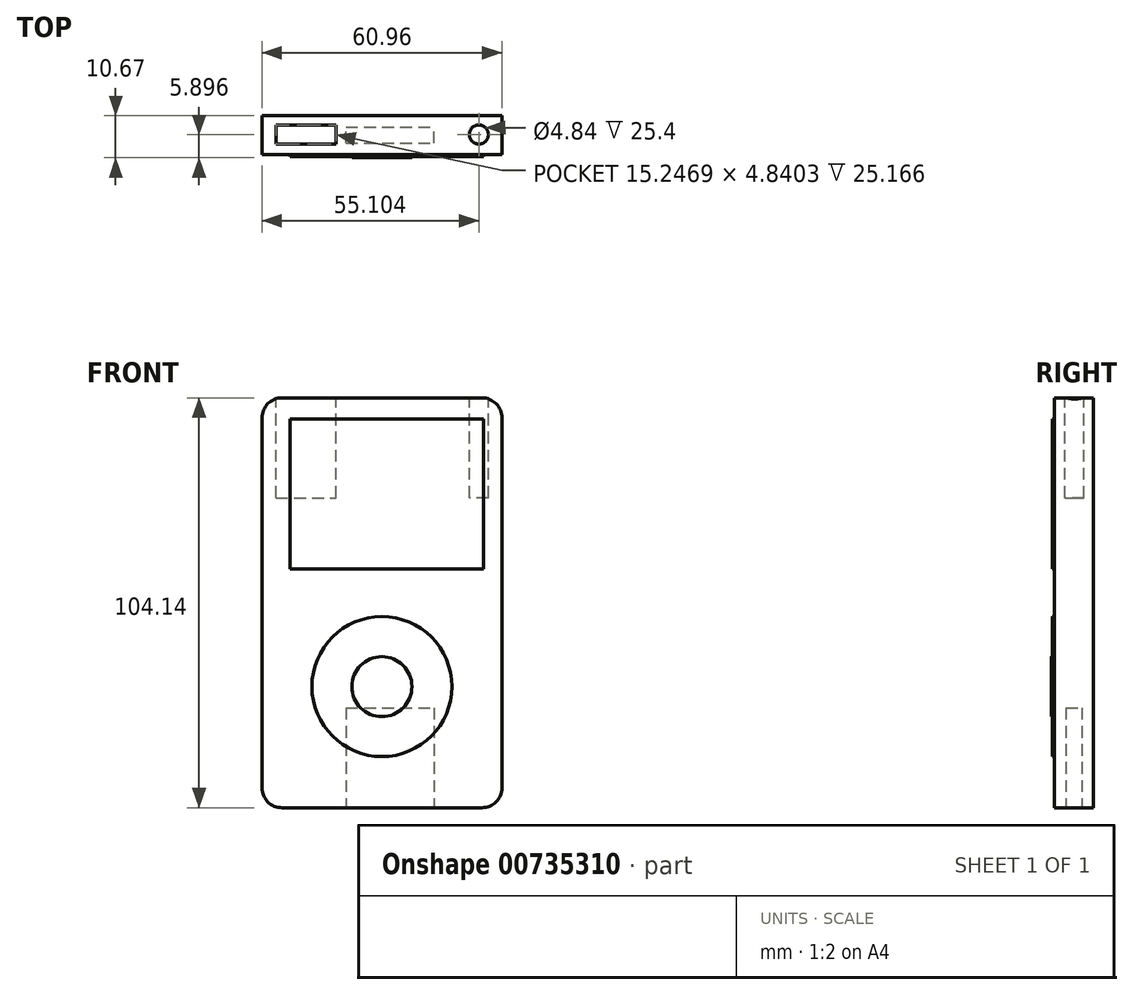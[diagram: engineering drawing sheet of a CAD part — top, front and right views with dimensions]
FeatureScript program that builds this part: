
annotation { "Feature Type Name" : "Feature", "Feature Type Description" : "" }
export const myFeature = defineFeature(function(context is Context, id is Id, definition is map)
    precondition{}
    {
        {
            var Q0;
            Q0=qCreatedBy(makeId("Front.planeOp"),FACE);
            var sketch = newSketch(context, id + "F0", { "sketchPlane" : qUnion([Q0])});
            skLineSegment(sketch, "E0.bottom", {"start": v(-21.34, 52.79) * mm, "end": v(39.62, 52.79) * mm});
            skLineSegment(sketch, "E0.top", {"start": v(-21.34, -51.35) * mm, "end": v(39.62, -51.35) * mm});
            skLineSegment(sketch, "E0.left", {"start": v(-21.34, 52.79) * mm, "end": v(-21.34, -51.35) * mm});
            skLineSegment(sketch, "E0.right", {"start": v(39.62, 52.79) * mm, "end": v(39.62, -51.35) * mm});
            skSolve(sketch);
        }
        {
            var Q0;
            Q0=makeQuery(id+"F0.imprint","IMPRINT",FACE,{"disambiguationData":[TD([[makeQuery(id+"F0.imprint","IMPRINT",EDGE,{"derivedFrom":sQuery(id+"F0.wireOp",EDGE,"E0.bottom")}),-1.0]])]});
            extrude(context, id + "F1", {"entities" : qUnion([Q0]), "depth" : 10.4 * mm, "offsetDistance" : 25.4 * mm});
        }
        {
            var Q0;
            Q0=makeQuery(id+"F1.opExtrude","CAP_FACE",FACE,{"disambiguationData":[OSD([sQuery(id+"F0.wireOp",EDGE,"E0.bottom"),sQuery(id+"F0.wireOp",EDGE,"E0.top"),sQuery(id+"F0.wireOp",EDGE,"E0.left"),sQuery(id+"F0.wireOp",EDGE,"E0.right")])],"isStart":false});
            var sketch = newSketch(context, id + "F2", { "sketchPlane" : qUnion([Q0])});
            skCircle(sketch, "E1", {"center": v(9.14, -20.58) * mm, "radius": 17.78 * mm});
            skLineSegment(sketch, "E2.bottom", {"start": v(-14.25, 47.45) * mm, "end": v(34.97, 47.45) * mm});
            skLineSegment(sketch, "E2.top", {"start": v(-14.25, 9.35) * mm, "end": v(34.97, 9.35) * mm});
            skLineSegment(sketch, "E2.left", {"start": v(-14.25, 47.45) * mm, "end": v(-14.25, 9.35) * mm});
            skLineSegment(sketch, "E2.right", {"start": v(34.97, 47.45) * mm, "end": v(34.97, 9.35) * mm});
            skSolve(sketch);
        }
        {
            var Q0;
            Q0=makeQuery(id+"F2.imprint","IMPRINT",FACE,{"disambiguationData":[TD([[makeQuery(id+"F2.imprint","IMPRINT",EDGE,{"derivedFrom":sQuery(id+"F2.wireOp",EDGE,"E1")}),-1.0]])]});
            extrude(context, id + "F3", {"entities" : qUnion([Q0]), "operationType" : NewBodyOperationType.REMOVE, "oppositeDirection" : true, "depth" : 0.5 * mm, "offsetDistance" : 25.4 * mm});
        }
        {
            var Q0;
            Q0=makeQuery(id+"F3.boolean.opBoolean","SPLIT",FACE,{"disambiguationData":[TD([makeQuery(id+"F3.opExtrude","SWEPT_FACE",FACE,{"disambiguationData":[OSD([sQuery(id+"F2.wireOp",EDGE,"E1")])]})])],"derivedFrom":makeQuery(id+"F1.opExtrude","CAP_FACE",FACE,{"disambiguationData":[OSD([sQuery(id+"F0.wireOp",EDGE,"E0.bottom"),sQuery(id+"F0.wireOp",EDGE,"E0.top"),sQuery(id+"F0.wireOp",EDGE,"E0.left"),sQuery(id+"F0.wireOp",EDGE,"E0.right")])],"isStart":false})});
            var sketch = newSketch(context, id + "F4", { "sketchPlane" : qUnion([Q0])});
            skCircle(sketch, "E3", {"center": v(9.14, -20.58) * mm, "radius": 7.62 * mm});
            skSolve(sketch);
        }
        {
            var Q0;
            Q0 = qSketchRegion(id + "F4", true);
            extrude(context, id + "F5", {"entities" : qUnion([Q0]), "operationType" : NewBodyOperationType.ADD, "depth" : 0.25 * mm, "offsetDistance" : 25.4 * mm});
        }
        {
            var Q0;
            Q0=makeQuery(id+"F1.opExtrude","SWEPT_FACE",FACE,{"disambiguationData":[OSD([sQuery(id+"F0.wireOp",EDGE,"E0.bottom")])]});
            var sketch = newSketch(context, id + "F6", { "sketchPlane" : qUnion([Q0])});
            skLineSegment(sketch, "E4.bottom", {"start": v(-17.79, -2.35) * mm, "end": v(-2.54, -2.35) * mm});
            skLineSegment(sketch, "E4.top", {"start": v(-17.79, -7.2) * mm, "end": v(-2.54, -7.2) * mm});
            skLineSegment(sketch, "E4.left", {"start": v(-17.79, -2.35) * mm, "end": v(-17.79, -7.2) * mm});
            skLineSegment(sketch, "E4.right", {"start": v(-2.54, -2.35) * mm, "end": v(-2.54, -7.2) * mm});
            skCircle(sketch, "E5", {"center": v(33.76, -4.77) * mm, "radius": 2.42 * mm});
            skSolve(sketch);
        }
        {
            var Q0;
            Q0=makeQuery(id+"F6.imprint","IMPRINT",FACE,{"disambiguationData":[TD([[makeQuery(id+"F6.imprint","IMPRINT",EDGE,{"derivedFrom":sQuery(id+"F6.wireOp",EDGE,"E4.bottom")}),-1.0]])]});
            var Q1;
            Q1=makeQuery(id+"F6.imprint","IMPRINT",FACE,{"disambiguationData":[TD([[makeQuery(id+"F6.imprint","IMPRINT",EDGE,{"derivedFrom":sQuery(id+"F6.wireOp",EDGE,"E5")}),1.0]])]});
            extrude(context, id + "F7", {"entities" : qUnion([Q0, Q1]), "operationType" : NewBodyOperationType.REMOVE, "oppositeDirection" : true, "depth" : 25.4 * mm, "offsetDistance" : 25.4 * mm});
        }
        {
            var Q0;
            Q0=makeQuery(id+"F1.opExtrude","SWEPT_EDGE",EDGE,{"disambiguationData":[OSD([sQuery(id+"F0.wireOp",EDGE,"E0.top"),sQuery(id+"F0.wireOp",EDGE,"E0.right")])]});
            var Q1;
            Q1=makeQuery(id+"F1.opExtrude","SWEPT_EDGE",EDGE,{"disambiguationData":[OSD([sQuery(id+"F0.wireOp",EDGE,"E0.top"),sQuery(id+"F0.wireOp",EDGE,"E0.left")])]});
            var Q2;
            Q2=makeQuery(id+"F1.opExtrude","SWEPT_EDGE",EDGE,{"disambiguationData":[OSD([sQuery(id+"F0.wireOp",EDGE,"E0.bottom"),sQuery(id+"F0.wireOp",EDGE,"E0.left")])]});
            var Q3;
            Q3=makeQuery(id+"F1.opExtrude","SWEPT_EDGE",EDGE,{"disambiguationData":[OSD([sQuery(id+"F0.wireOp",EDGE,"E0.bottom"),sQuery(id+"F0.wireOp",EDGE,"E0.right")])]});
            fillet(context, id + "F8", {"entities" : qUnion([Q0, Q1, Q2, Q3]), "radius" : 5.08 * mm, "tangentPropagation" : true, "allowEdgeOverflow" : false});
        }
        {
            var Q0;
            Q0=makeQuery(id+"F1.opExtrude","SWEPT_FACE",FACE,{"disambiguationData":[OSD([sQuery(id+"F0.wireOp",EDGE,"E0.top")])]});
            var sketch = newSketch(context, id + "F9", { "sketchPlane" : qUnion([Q0])});
            skLineSegment(sketch, "E6.bottom", {"start": v(0, 6.97) * mm, "end": v(22.34, 6.97) * mm});
            skLineSegment(sketch, "E6.top", {"start": v(0, 2.9) * mm, "end": v(22.34, 2.9) * mm});
            skLineSegment(sketch, "E6.left", {"start": v(0, 6.97) * mm, "end": v(0, 2.9) * mm});
            skLineSegment(sketch, "E6.right", {"start": v(22.34, 6.97) * mm, "end": v(22.34, 2.9) * mm});
            skSolve(sketch);
        }
        {
            var Q0;
            Q0=makeQuery(id+"F9.imprint","IMPRINT",FACE,{"disambiguationData":[TD([[makeQuery(id+"F9.imprint","IMPRINT",EDGE,{"derivedFrom":sQuery(id+"F9.wireOp",EDGE,"E6.bottom")}),-1.0]])]});
            extrude(context, id + "F10", {"entities" : qUnion([Q0]), "operationType" : NewBodyOperationType.REMOVE, "oppositeDirection" : true, "depth" : 25.4 * mm, "offsetDistance" : 25.4 * mm});
        }
    });
